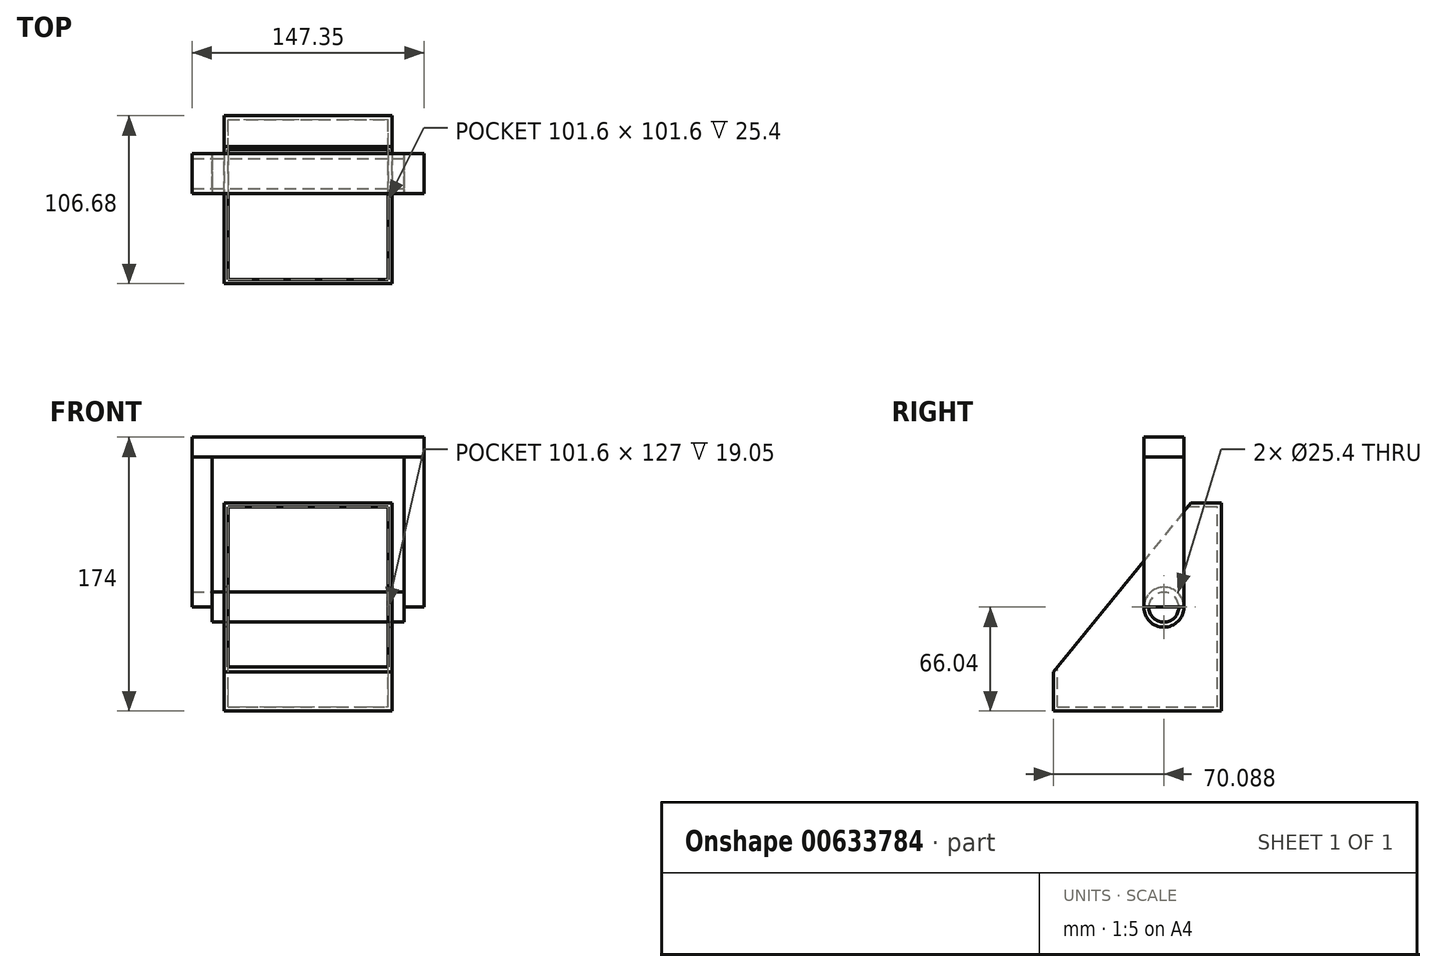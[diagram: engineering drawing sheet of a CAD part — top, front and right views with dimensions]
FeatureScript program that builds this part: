
annotation { "Feature Type Name" : "Feature", "Feature Type Description" : "" }
export const myFeature = defineFeature(function(context is Context, id is Id, definition is map)
    precondition{}
    {
        {
            var Q0;
            Q0=qCreatedBy(makeId("Right.planeOp"),FACE);
            var sketch = newSketch(context, id + "F0", { "sketchPlane" : qUnion([Q0])});
            skLineSegment(sketch, "E0", {"start": v(0, 0) * mm, "end": v(101.6, 0) * mm});
            skLineSegment(sketch, "E1", {"start": v(101.6, 0) * mm, "end": v(101.6, 127) * mm});
            skLineSegment(sketch, "E2", {"start": v(101.6, 127) * mm, "end": v(82.55, 127) * mm});
            skLineSegment(sketch, "E3", {"start": v(0, 0) * mm, "end": v(0, 25.4) * mm});
            skLineSegment(sketch, "E4", {"start": v(82.55, 127) * mm, "end": v(0, 25.4) * mm});
            skSolve(sketch);
        }
        {
            var Q0;
            Q0 = qSketchRegion(id + "F0", true);
            extrude(context, id + "F1", {"entities" : qUnion([Q0]), "oppositeDirection" : true, "depth" : 101.6 * mm, "offsetDistance" : 25.4 * mm});
        }
        {
            var Q0;
            Q0=makeQuery(id+"F1.opExtrude","SWEPT_FACE",FACE,{"disambiguationData":[OSD([sQuery(id+"F0.wireOp",EDGE,"E4")])]});
            shell(context, id + "F2", {"entities" : qUnion([Q0]), "thickness" : 2.54 * mm, "oppositeDirection" : true});
        }
        {
            var Q0;
            Q0=makeQuery(id+"F1.opExtrude","CAP_FACE",FACE,{"disambiguationData":[OSD([sQuery(id+"F0.wireOp",EDGE,"E0"),sQuery(id+"F0.wireOp",EDGE,"E1"),sQuery(id+"F0.wireOp",EDGE,"E2"),sQuery(id+"F0.wireOp",EDGE,"E3"),sQuery(id+"F0.wireOp",EDGE,"E4")])],"isStart":true});
            var sketch = newSketch(context, id + "F3", { "sketchPlane" : qUnion([Q0])});
            skCircle(sketch, "E5", {"center": v(67.55, 63.5) * mm, "radius": 12.7 * mm});
            skSolve(sketch);
        }
        {
            var Q0;
            Q0=makeQuery(id+"F3.imprint","IMPRINT",FACE,{"disambiguationData":[TD([[makeQuery(id+"F3.imprint","IMPRINT",EDGE,{"derivedFrom":sQuery(id+"F3.wireOp",EDGE,"E5")}),1.0]])]});
            extrude(context, id + "F4", {"entities" : qUnion([Q0]), "operationType" : NewBodyOperationType.REMOVE, "oppositeDirection" : true, "depth" : 101.6 * mm, "offsetDistance" : 25.4 * mm});
        }
        {
            var Q0;
            Q0=makeQuery(id+"F1.opExtrude","CAP_FACE",FACE,{"disambiguationData":[OSD([sQuery(id+"F0.wireOp",EDGE,"E0"),sQuery(id+"F0.wireOp",EDGE,"E1"),sQuery(id+"F0.wireOp",EDGE,"E2"),sQuery(id+"F0.wireOp",EDGE,"E3"),sQuery(id+"F0.wireOp",EDGE,"E4")])],"isStart":false});
            var sketch = newSketch(context, id + "F5", { "sketchPlane" : qUnion([Q0])});
            skCircle(sketch, "E6", {"center": v(-67.55, 63.5) * mm, "radius": 12.7 * mm});
            skSolve(sketch);
        }
        {
            var Q0;
            Q0=makeQuery(id+"F5.imprint","IMPRINT",FACE,{"disambiguationData":[TD([[makeQuery(id+"F5.imprint","IMPRINT",EDGE,{"derivedFrom":sQuery(id+"F5.wireOp",EDGE,"E6")}),1.0]])]});
            extrude(context, id + "F6", {"entities" : qUnion([Q0]), "operationType" : NewBodyOperationType.REMOVE, "oppositeDirection" : true, "depth" : 101.6 * mm, "offsetDistance" : 25.4 * mm});
        }
        {
            var Q0;
            Q0=makeQuery(id+"F1.opExtrude","CAP_FACE",FACE,{"disambiguationData":[OSD([sQuery(id+"F0.wireOp",EDGE,"E0"),sQuery(id+"F0.wireOp",EDGE,"E1"),sQuery(id+"F0.wireOp",EDGE,"E2"),sQuery(id+"F0.wireOp",EDGE,"E3"),sQuery(id+"F0.wireOp",EDGE,"E4")])],"isStart":true});
            var sketch = newSketch(context, id + "F7", { "sketchPlane" : qUnion([Q0])});
            skCircle(sketch, "E7", {"center": v(67.55, 63.5) * mm, "radius": 9.53 * mm});
            skSolve(sketch);
        }
        {
            var Q0;
            Q0=makeQuery(id+"F7.imprint","IMPRINT",FACE,{"disambiguationData":[TD([[makeQuery(id+"F7.imprint","IMPRINT",EDGE,{"derivedFrom":sQuery(id+"F7.wireOp",EDGE,"E7")}),1.0]])]});
            extrude(context, id + "F8", {"entities" : qUnion([Q0]), "oppositeDirection" : true, "depth" : 114.3 * mm, "offsetDistance" : 25.4 * mm});
        }
        {
            var Q0;
            Q0=makeQuery(id+"F8.opExtrude","CAP_FACE",FACE,{"disambiguationData":[OSD([sQuery(id+"F7.wireOp",EDGE,"E7")])],"isStart":true});
            extrude(context, id + "F9", {"entities" : qUnion([Q0]), "operationType" : NewBodyOperationType.ADD, "depth" : 7.62 * mm, "offsetDistance" : 25.4 * mm});
        }
        {
            var Q0;
            Q0=makeQuery(id+"F9.opExtrude","CAP_FACE",FACE,{"disambiguationData":[OSD([sQuery(id+"F7.wireOp",EDGE,"E7")])],"isStart":false});
            var sketch = newSketch(context, id + "F10", { "sketchPlane" : qUnion([Q0])});
            skLineSegment(sketch, "E8", {"start": v(67.55, 63.5) * mm, "end": v(80.25, 63.5) * mm});
            skLineSegment(sketch, "E9", {"start": v(67.55, 63.5) * mm, "end": v(54.85, 63.5) * mm});
            skLineSegment(sketch, "E10", {"start": v(54.85, 63.5) * mm, "end": v(54.85, 158.75) * mm});
            skLineSegment(sketch, "E11", {"start": v(80.25, 63.5) * mm, "end": v(80.25, 158.75) * mm});
            skLineSegment(sketch, "E12", {"start": v(80.25, 158.75) * mm, "end": v(54.85, 158.75) * mm});
            skSolve(sketch);
        }
        {
            var Q0;
            Q0 = qSketchRegion(id + "F10", true);
            extrude(context, id + "F11", {"entities" : qUnion([Q0]), "operationType" : NewBodyOperationType.ADD, "depth" : 12.7 * mm, "offsetDistance" : 25.4 * mm});
        }
        {
            var Q0;
            Q0=makeQuery(id+"F8.opExtrude","CAP_FACE",FACE,{"disambiguationData":[OSD([sQuery(id+"F7.wireOp",EDGE,"E7")])],"isStart":false});
            var sketch = newSketch(context, id + "F12", { "sketchPlane" : qUnion([Q0])});
            skLineSegment(sketch, "E13", {"start": v(-67.55, 63.5) * mm, "end": v(-80.25, 63.5) * mm});
            skLineSegment(sketch, "E14", {"start": v(-67.55, 63.5) * mm, "end": v(-54.85, 63.5) * mm});
            skLineSegment(sketch, "E15", {"start": v(-80.25, 63.5) * mm, "end": v(-80.25, 158.76) * mm});
            skLineSegment(sketch, "E16", {"start": v(-80.25, 158.76) * mm, "end": v(-54.85, 158.76) * mm});
            skLineSegment(sketch, "E17", {"start": v(-54.85, 158.76) * mm, "end": v(-54.85, 63.5) * mm});
            skSolve(sketch);
        }
        {
            var Q0;
            {var subQ0=sQuery(id+"F12.wireOp",EDGE,"E15");Q0=makeQuery(id+"F12.imprint","IMPRINT",FACE,{"disambiguationData":[TD([[makeQuery(id+"F12.imprint","IMPRINT",EDGE,{"derivedFrom":subQ0}),-1.0]])]});}
            extrude(context, id + "F13", {"entities" : qUnion([Q0]), "depth" : 12.7 * mm, "offsetDistance" : 25.4 * mm});
        }
        {
            var Q0;
            Q0=makeQuery(id+"F13.opExtrude","CAP_FACE",FACE,{"disambiguationData":[OSD([sQuery(id+"F7.wireOp",EDGE,"E7"),sQuery(id+"F12.wireOp",EDGE,"E13"),sQuery(id+"F12.wireOp",EDGE,"E14"),sQuery(id+"F12.wireOp",EDGE,"E15"),sQuery(id+"F12.wireOp",EDGE,"E16"),sQuery(id+"F12.wireOp",EDGE,"E17")])],"isStart":false});
            var sketch = newSketch(context, id + "F14", { "sketchPlane" : qUnion([Q0])});
            skLineSegment(sketch, "E18", {"start": v(-77.07, 63.5) * mm, "end": v(-58.02, 63.5) * mm});
            skSolve(sketch);
        }
        {
            var Q0;
            Q0=makeQuery(id+"F14.imprint","IMPRINT",FACE,{"disambiguationData":[TD([[makeQuery(id+"F14.imprint","IMPRINT",EDGE,{"derivedFrom":sQuery(id+"F14.wireOp",EDGE,"E18")}),1.0]])]});
            extrude(context, id + "F15", {"entities" : qUnion([Q0]), "depth" : 0.03 * mm, "offsetDistance" : 25.4 * mm});
        }
        {
            var Q0;
            Q0=makeQuery(id+"F13.opExtrude","SWEPT_FACE",FACE,{"disambiguationData":[OSD([sQuery(id+"F12.wireOp",EDGE,"E17")])]});
            var sketch = newSketch(context, id + "F16", { "sketchPlane" : qUnion([Q0])});
            skLineSegment(sketch, "E19", {"start": v(-124.46, 158.76) * mm, "end": v(-124.46, 171.46) * mm});
            skLineSegment(sketch, "E20", {"start": v(-124.46, 171.46) * mm, "end": v(22.86, 171.46) * mm});
            skLineSegment(sketch, "E21", {"start": v(22.86, 171.46) * mm, "end": v(22.86, 158.76) * mm});
            skLineSegment(sketch, "E22", {"start": v(22.86, 158.76) * mm, "end": v(-124.46, 158.76) * mm});
            skSolve(sketch);
        }
        {
            var Q0;
            {var subQ4=sQuery(id+"F16.wireOp",EDGE,"E19");Q0=makeQuery(id+"F16.imprint","IMPRINT",FACE,{"disambiguationData":[TD([[makeQuery(id+"F16.imprint","IMPRINT",EDGE,{"derivedFrom":subQ4}),-1.0]])]});}
            extrude(context, id + "F17", {"entities" : qUnion([Q0]), "oppositeDirection" : true, "depth" : 25.4 * mm, "offsetDistance" : 25.4 * mm});
        }
    });
